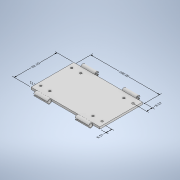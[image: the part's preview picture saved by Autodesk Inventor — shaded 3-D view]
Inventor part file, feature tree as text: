
AUTODESK INVENTOR PART (.ipt)
format: ipt  version: 2020 (Build 240168000, 168)  size: 275,456 bytes
history: native  units: mm
features: sketch x9, hole x8, other x7, extrude x6
ambient origin geometry x8: Origin, YZ Plane, XZ Plane, XY Plane, X Axis, Y Axis, Z Axis, Center Point
bodies: Solid1 (feature_tree)
feature tree (30):
  other  "Annotations"
  extrude  "Extrusion1"  Depth=62.1mm
  extrude  "Extrusion2"  Depth=40.0mm TaperAngle=0.0deg
  extrude  "Extrusion3"  Depth=0.001mm TaperAngle=0.0deg
  extrude  "Extrusion4"  Depth=10.0mm TaperAngle=0.0deg
  extrude  "Extrusion5"  Depth=100.0mm
  extrude  "Extrusion6"  Depth=100.0mm
  hole  "Hole5"  [1 undecoded]
  hole  "Hole6"  [1 undecoded]
  hole  "Hole7"  [1 undecoded]
  hole  "Hole8"  [1 undecoded]
  hole  "Hole10"  [1 undecoded]
  hole  "Hole9"  [1 undecoded]
  hole  "Hole12"  [1 undecoded]
  hole  "Hole11"  [1 undecoded]
  sketch  "Sketch1"  dims[d0=2.9mm d1=62.1mm]
  sketch  "Sketch4"  dims[d4=20.0mm d5=0.0mm d6=40.0mm d7=0.0mm]
  sketch  "Sketch9"  dims[d8=20.0mm d9=0.0mm d50=0.001mm d51=0.0mm]
  sketch  "Sketch14"  dims[d61=10.0mm d62=0.0mm d63=10.0mm d64=0.0mm]
  sketch  "Sketch15"  dims[d65=2.921mm d66=6.0mm d67=4.0mm d68=2.0mm d69=90.0deg d70=8.0mm d71=20.594885mm]
  sketch  "Sketch16"  dims[d84=2.921mm d85=6.0mm d86=4.0mm d87=2.0mm d88=90.0deg d89=8.0mm d90=20.594885mm]
  sketch  "Sketch17"  dims[d91=2.921mm d92=6.0mm d93=4.0mm d94=2.0mm d95=90.0deg d96=8.0mm d97=20.594885mm]
  sketch  "Sketch18"  dims[d98=2.921mm d99=6.0mm d100=4.0mm d101=2.0mm d102=90.0deg d103=8.0mm d104=20.594885mm]
  sketch  "Sketch19"  dims[d105=2.921mm d106=6.0mm d107=4.0mm d108=2.0mm d109=90.0deg d110=8.0mm d111=20.594885mm d112=2.921mm d113=6.0mm d114=4.0mm d115=2.0mm d116=90.0deg d117=8.0mm d118=20.594885mm d119=2.921mm d120=6.0mm d121=4.0mm d122=2.0mm d123=90.0deg d124=8.0mm d125=20.594885mm d126=2.921mm d127=6.0mm d128=4.0mm d129=2.0mm d130=90.0deg d131=8.0mm d132=20.594885mm d133=8.57mm d134=5.41mm d135=8.57mm d136=13.26mm d137=5.41mm d138=44.96mm d139=44.96mm d140=44.96mm d141=44.96mm d142=5.41mm d143=5.41mm d144=13.26mm d145=13.26mm d146=8.57mm d147=8.57mm d148=13.26mm d163=1.1mm d164=1.1mm d165=2.2mm d166=2.29907mm d167=3.3mm d168=3.3mm d171=6.062961mm d172=6.104896mm d174=6.063mm d176=1.1mm d177=1.1mm d178=2.2mm d150=13.26mm d151=44.96mm d154=5.128261mm d155=8.57mm d180=5.063866mm d181=8.57mm d182=5.882722mm d183=5.186499mm d184=62.1mm d72=1.978463mm d73=6.235219mm d74=100.0mm]
  other  "Linear Dimension 6"
  other  "Linear Dimension 11"
  other  "Linear Dimension 12"
  other  "Linear Dimension 14"
  other  "Linear Dimension 15"
  other  "Linear Dimension 16"
note: 8 required parameter values undecoded (feature->parameter linkage not recoverable at this tier; creation-order binding heuristic only, values carry confidence <= 0.55)
